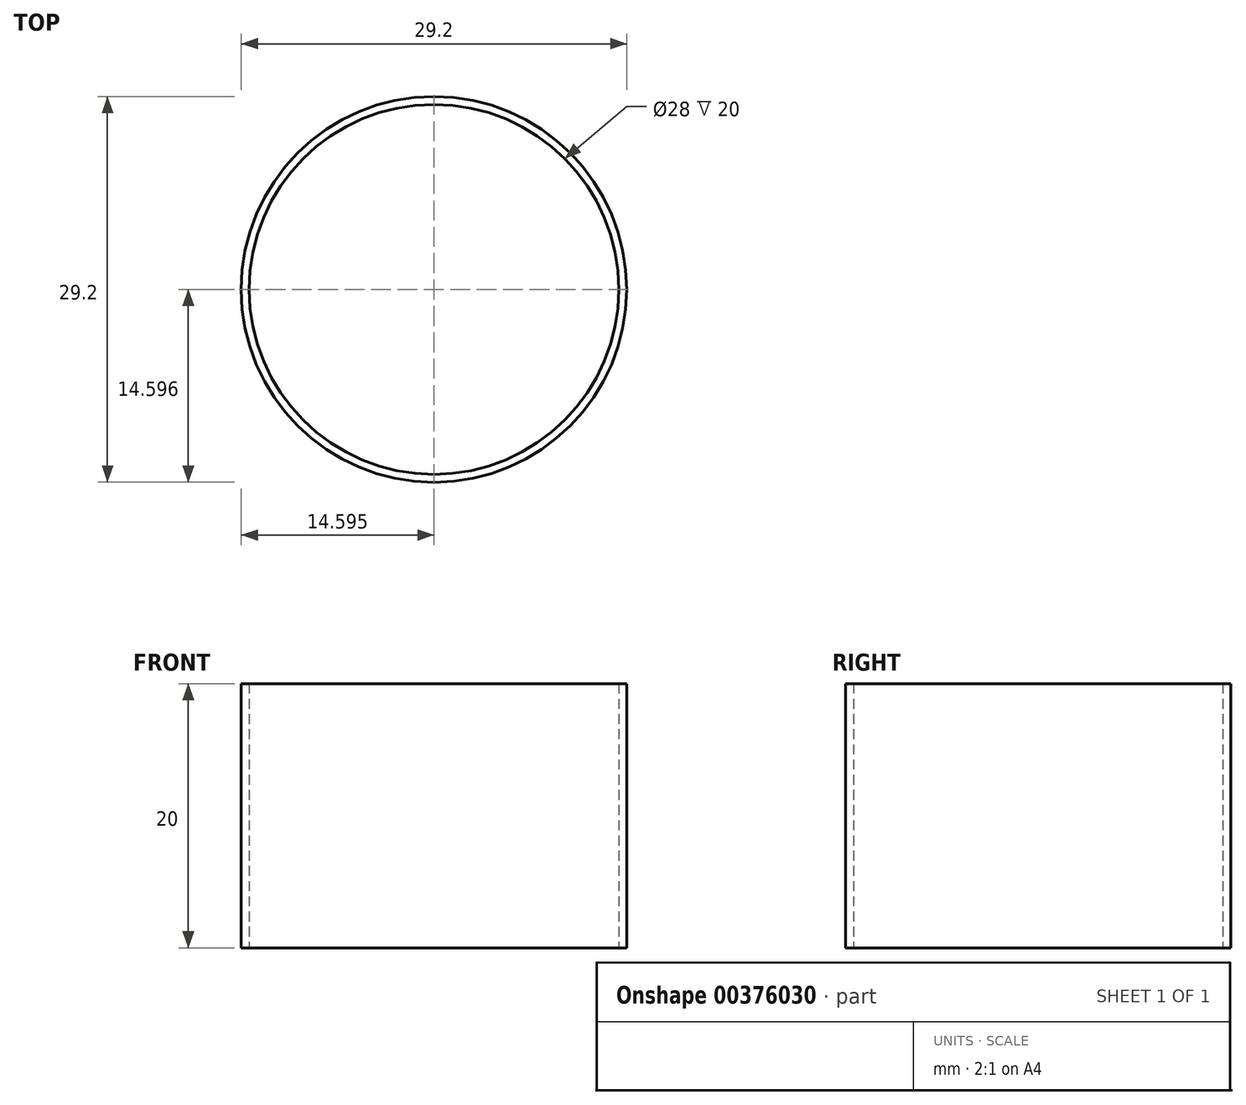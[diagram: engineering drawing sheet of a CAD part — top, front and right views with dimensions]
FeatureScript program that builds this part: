
annotation { "Feature Type Name" : "Feature", "Feature Type Description" : "" }
export const myFeature = defineFeature(function(context is Context, id is Id, definition is map)
    precondition{}
    {
        {
            var Q0;
            Q0=qCreatedBy(makeId("Top.planeOp"),FACE);
            var sketch = newSketch(context, id + "F0", { "sketchPlane" : qUnion([Q0])});
            skCircle(sketch, "E0", {"center": v(-9.21, 8.78) * mm, "radius": 14.6 * mm});
            skCircle(sketch, "E1", {"center": v(-9.21, 8.78) * mm, "radius": 14 * mm});
            skSolve(sketch);
        }
        {
            var Q0;
            Q0=makeQuery(id+"F0.imprint","IMPRINT",FACE,{"disambiguationData":[TD([[makeQuery(id+"F0.imprint","IMPRINT",EDGE,{"derivedFrom":sQuery(id+"F0.wireOp",EDGE,"E0")}),1.0]])]});
            var Q1;
            Q1=sQuery(id+"F0.wireOp",EDGE,"E0");
            extrude(context, id + "F1", {"entities" : qUnion([Q0]), "surfaceEntities" : qUnion([Q1]), "depth" : 20 * mm});
        }
    });
